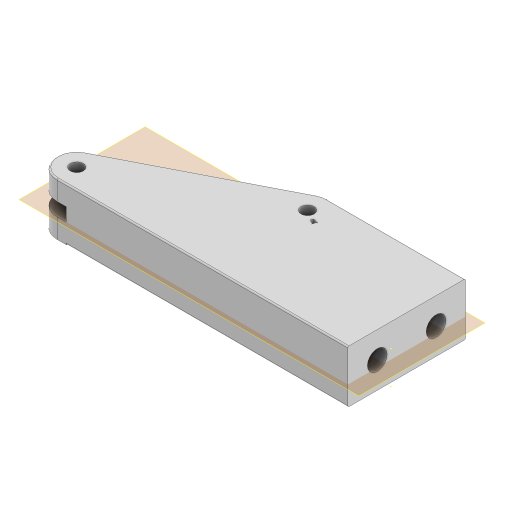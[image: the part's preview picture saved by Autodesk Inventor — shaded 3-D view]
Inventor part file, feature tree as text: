
AUTODESK INVENTOR PART (.ipt)
format: ipt  version: 2024 (Build 280153000, 153)  size: 265,728 bytes
history: native  units: mm
features: sketch x10, extrude x9, fillet x6, plane x3
ambient origin geometry x8: Origin, YZ Plane, XZ Plane, XY Plane, X Axis, Y Axis, Z Axis, Center Point
bodies: Solid1 (feature_tree)
feature tree (28):
  sketch  "Sketch1"  dims[d0=10.0mm d1=10.0mm d3=59.4mm]
  extrude  "Extrusion1"  Depth=10.0mm
  fillet  "Fillet1"  Radius=59.4mm
  extrude  "Extrusion2"  Depth=15.0mm
  sketch  "Sketch4"  dims[d6=15.0mm d7=15.0mm]
  extrude  "Extrusion5"  Depth=15.0mm
  extrude  "Extrusion6"  Depth=15.0mm
  fillet  "Fillet3"  Radius=15.0mm
  sketch  "Sketch5"  dims[d8=40.0mm d9=0.0mm d10=15.0mm d12=15.0mm]
  extrude  "Extrusion7"  Depth=15.0mm
  extrude  "Extrusion8"  Depth=30.0mm TaperAngle=0.0deg
  sketch  "Sketch7"  dims[d13=22.35mm d14=15.0mm]
  plane  "Work Plane1"
  extrude  "Extrusion9"  Depth=25.0mm TaperAngle=0.0deg
  plane  "Work Plane2"
  extrude  "Extrusion10"  Depth=116.1mm
  fillet  "Fillet4"  Radius=105.0mm
  fillet  "Fillet5"  Radius=283.350776mm
  fillet  "Fillet6"  Radius=1.0mm
  fillet  "Fillet7"  Radius=22.0mm
  sketch  "Sketch10"  dims[d28=15.0mm d29=0.0mm d32=116.1mm d33=105.0mm d34=283.350776mm d35=1.0mm d36=22.0mm]
  plane  "Work Plane3"
  sketch  "Sketch13"  dims[d37=20.495401mm d38=25.0mm d39=0.0mm]
  extrude  "Extrusion11"  Depth=25.0mm TaperAngle=0.0deg
  sketch  "Sketch2"  dims[d4=89.4mm d5=15.0mm]
  sketch  "Sketch8"  dims[d15=22.35mm d16=30.0mm d17=0.0mm]
  sketch  "Sketch9"  dims[d23=19.010126mm d26=25.0mm d27=0.0mm]
  sketch  "Sketch14"  dims[d40=15.0mm d41=0.0mm d44=90.0deg d45=26.5mm d46=28.0mm d47=0.0mm d48=90.0deg d49=26.0mm d50=18.0mm d51=0.0mm d52=5.0mm d53=5.0mm d54=5.0mm d55=5.0mm d56=-25.0mm d59=-1.594mm d60=-3.599316mm d61=-3.810496mm d62=-3.050618mm d63=0.0mm d64=0.0mm d42=0.5mm d43=0.872665mm d57=0.0mm d58=0.872665mm d65=0.5mm d66=0.872665mm d67=0.5mm d68=0.872665mm]
